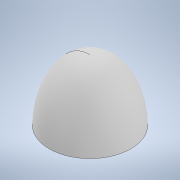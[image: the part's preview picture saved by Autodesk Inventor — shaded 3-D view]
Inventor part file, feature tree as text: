
AUTODESK INVENTOR PART (.ipt)
format: ipt  version: 2022 (Build 260153000, 153)  size: 236,032 bytes
history: native  units: in
note: dims shown in document units (in); Inventor stores cm internally (conversion verified against a paired STEP export)
features: revolve x1, shell x1, sketch x1
ambient origin geometry x8: Origin, YZ Plane, XZ Plane, XY Plane, X Axis, Y Axis, Z Axis, Center Point
bodies: Solid1 (feature_tree)
feature tree (3):
  revolve  "Revolution1"  [1 undecoded]
  shell  "Shell1"  [1 undecoded]
  sketch  "Sketch1"  dims[d3=90.0deg d4=0.25in]
note: 2 required parameter values undecoded (feature->parameter linkage not recoverable at this tier; creation-order binding heuristic only, values carry confidence <= 0.55)